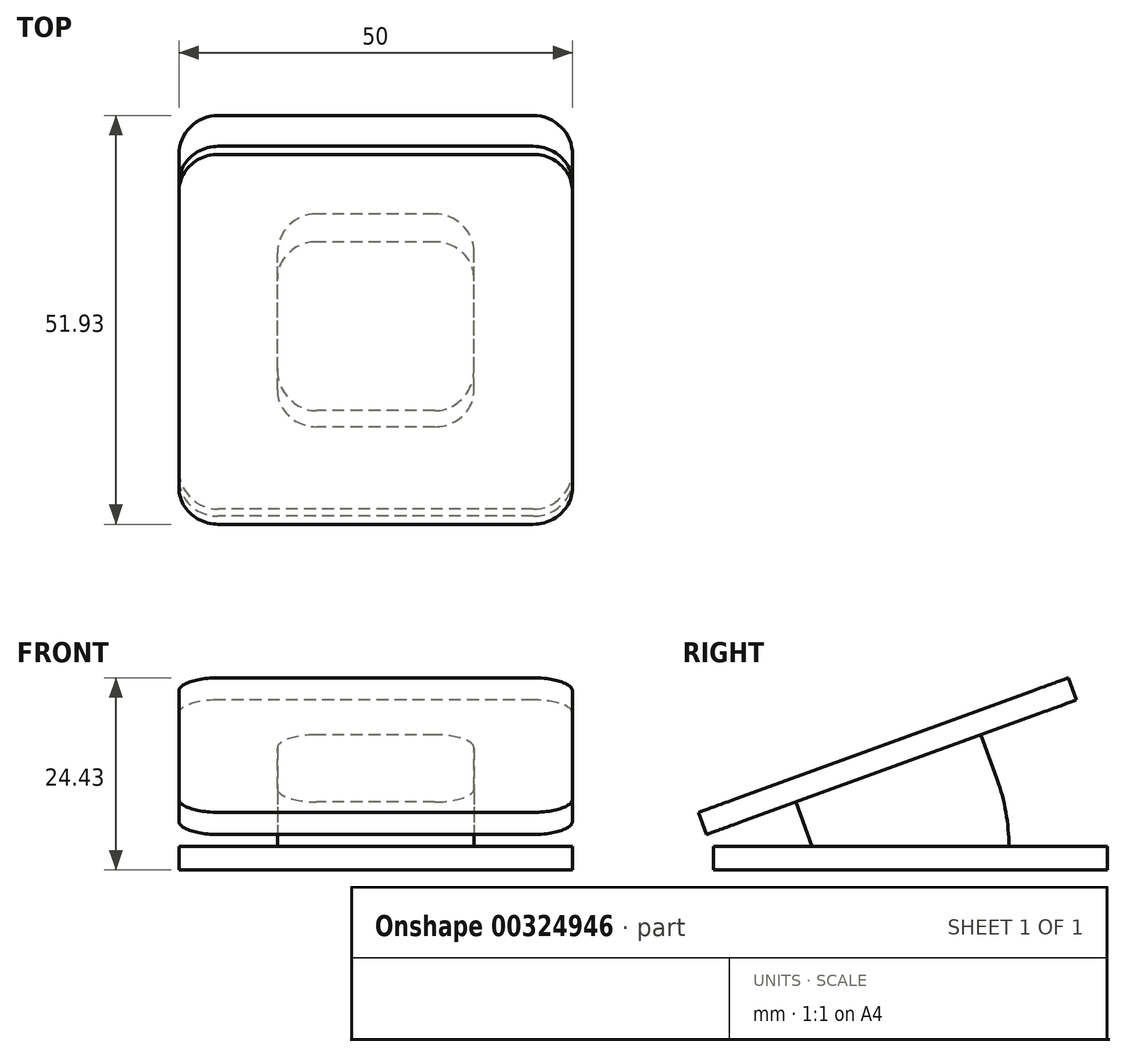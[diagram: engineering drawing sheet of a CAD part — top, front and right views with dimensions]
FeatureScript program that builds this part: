
annotation { "Feature Type Name" : "Feature", "Feature Type Description" : "" }
export const myFeature = defineFeature(function(context is Context, id is Id, definition is map)
    precondition{}
    {
        {
            var Q0;
            Q0=qCreatedBy(makeId("Top.planeOp"),FACE);
            var sketch = newSketch(context, id + "F0", { "sketchPlane" : qUnion([Q0])});
            skLineSegment(sketch, "E0.bottom", {"start": v(25, -25) * mm, "end": v(-25, -25) * mm});
            skLineSegment(sketch, "E0.top", {"start": v(25, 25) * mm, "end": v(-25, 25) * mm});
            skLineSegment(sketch, "E0.left", {"start": v(25, -25) * mm, "end": v(25, 25) * mm});
            skLineSegment(sketch, "E0.right", {"start": v(-25, -25) * mm, "end": v(-25, 25) * mm});
            skPoint(sketch, "E0.middle", {"position": v(0, 0) * mm});
            skSolve(sketch);
        }
        {
            var Q0;
            Q0=makeQuery(id+"F0.imprint","IMPRINT",FACE,{"disambiguationData":[TD([[makeQuery(id+"F0.imprint","IMPRINT",EDGE,{"derivedFrom":sQuery(id+"F0.wireOp",EDGE,"E0.bottom")}),-1.0]])]});
            extrude(context, id + "F1", {"entities" : qUnion([Q0]), "depth" : 3 * mm});
        }
        {
            var Q0;
            Q0=makeQuery(id+"F1.opExtrude","CAP_FACE",FACE,{"disambiguationData":[OSD([sQuery(id+"F0.wireOp",EDGE,"E0.bottom"),sQuery(id+"F0.wireOp",EDGE,"E0.top"),sQuery(id+"F0.wireOp",EDGE,"E0.left"),sQuery(id+"F0.wireOp",EDGE,"E0.right")])],"isStart":false});
            var sketch = newSketch(context, id + "F2", { "sketchPlane" : qUnion([Q0])});
            skLineSegment(sketch, "E1.bottom", {"start": v(12.5, -12.5) * mm, "end": v(-12.5, -12.5) * mm});
            skLineSegment(sketch, "E1.top", {"start": v(12.5, 12.5) * mm, "end": v(-12.5, 12.5) * mm});
            skLineSegment(sketch, "E1.left", {"start": v(12.5, -12.5) * mm, "end": v(12.5, 12.5) * mm});
            skLineSegment(sketch, "E1.right", {"start": v(-12.5, -12.5) * mm, "end": v(-12.5, 12.5) * mm});
            skPoint(sketch, "E1.middle", {"position": v(0, 0) * mm});
            skSolve(sketch);
        }
        {
            var Q0;
            Q0=makeQuery(id+"F2.imprint","IMPRINT",FACE,{"disambiguationData":[TD([[makeQuery(id+"F2.imprint","IMPRINT",EDGE,{"derivedFrom":sQuery(id+"F2.wireOp",EDGE,"E1.bottom")}),-1.0]])]});
            var Q1;
            Q1=sQuery(id+"F2.wireOp",EDGE,"E1.bottom");
            revolve(context, id + "F3", {"operationType" : NewBodyOperationType.ADD, "entities" : qUnion([Q0]), "axis" : qUnion([Q1]), "revolveType" : RevolveType.ONE_DIRECTION, "oppositeDirection" : true, "angle" : 20 * degree});
        }
        {
            var Q0;
            Q0=makeQuery(id+"F3.opRevolve","CAP_FACE",FACE,{"disambiguationData":[OSD([sQuery(id+"F2.wireOp",EDGE,"E1.bottom"),sQuery(id+"F2.wireOp",EDGE,"E1.top"),sQuery(id+"F2.wireOp",EDGE,"E1.left"),sQuery(id+"F2.wireOp",EDGE,"E1.right")])],"isStart":false});
            extrude(context, id + "F4", {"entities" : qUnion([Q0]), "operationType" : NewBodyOperationType.ADD, "depth" : 6 * mm});
        }
        {
            var Q0;
            Q0=makeQuery(id+"F4.opExtrude","CAP_FACE",FACE,{"disambiguationData":[OSD([sQuery(id+"F2.wireOp",EDGE,"E1.bottom"),sQuery(id+"F2.wireOp",EDGE,"E1.top"),sQuery(id+"F2.wireOp",EDGE,"E1.left"),sQuery(id+"F2.wireOp",EDGE,"E1.right")])],"isStart":false});
            var sketch = newSketch(context, id + "F5", { "sketchPlane" : qUnion([Q0])});
            skLineSegment(sketch, "E2.bottom", {"start": v(25, -22.8) * mm, "end": v(-25, -22.8) * mm});
            skLineSegment(sketch, "E2.top", {"start": v(25, 27.2) * mm, "end": v(-25, 27.2) * mm});
            skLineSegment(sketch, "E2.left", {"start": v(25, -22.8) * mm, "end": v(25, 27.2) * mm});
            skLineSegment(sketch, "E2.right", {"start": v(-25, -22.8) * mm, "end": v(-25, 27.2) * mm});
            skPoint(sketch, "E2.middle", {"position": v(0, 2.2) * mm});
            skSolve(sketch);
        }
        {
            var Q0;
            Q0 = qSketchRegion(id + "F5", true);
            extrude(context, id + "F6", {"entities" : qUnion([Q0]), "operationType" : NewBodyOperationType.ADD, "depth" : 3 * mm});
        }
        {
            var Q0;
            Q0=makeQuery(id+"F6.opExtrude","SWEPT_EDGE",EDGE,{"disambiguationData":[OSD([sQuery(id+"F5.wireOp",EDGE,"E2.top"),sQuery(id+"F5.wireOp",EDGE,"E2.left")])]});
            var Q1;
            Q1=makeQuery(id+"F6.opExtrude","SWEPT_EDGE",EDGE,{"disambiguationData":[OSD([sQuery(id+"F5.wireOp",EDGE,"E2.top"),sQuery(id+"F5.wireOp",EDGE,"E2.right")])]});
            var Q2;
            Q2=makeQuery(id+"F6.opExtrude","SWEPT_EDGE",EDGE,{"disambiguationData":[OSD([sQuery(id+"F5.wireOp",EDGE,"E2.bottom"),sQuery(id+"F5.wireOp",EDGE,"E2.right")])]});
            var Q3;
            Q3=makeQuery(id+"F6.opExtrude","SWEPT_EDGE",EDGE,{"disambiguationData":[OSD([sQuery(id+"F5.wireOp",EDGE,"E2.bottom"),sQuery(id+"F5.wireOp",EDGE,"E2.left")])]});
            var Q4;
            Q4=makeQuery(id+"F1.opExtrude","SWEPT_EDGE",EDGE,{"disambiguationData":[OSD([sQuery(id+"F0.wireOp",EDGE,"E0.bottom"),sQuery(id+"F0.wireOp",EDGE,"E0.left")])]});
            var Q5;
            Q5=makeQuery(id+"F1.opExtrude","SWEPT_EDGE",EDGE,{"disambiguationData":[OSD([sQuery(id+"F0.wireOp",EDGE,"E0.bottom"),sQuery(id+"F0.wireOp",EDGE,"E0.right")])]});
            var Q6;
            Q6=makeQuery(id+"F1.opExtrude","SWEPT_EDGE",EDGE,{"disambiguationData":[OSD([sQuery(id+"F0.wireOp",EDGE,"E0.top"),sQuery(id+"F0.wireOp",EDGE,"E0.right")])]});
            var Q7;
            Q7=makeQuery(id+"F1.opExtrude","SWEPT_EDGE",EDGE,{"disambiguationData":[OSD([sQuery(id+"F0.wireOp",EDGE,"E0.top"),sQuery(id+"F0.wireOp",EDGE,"E0.left")])]});
            fillet(context, id + "F7", {"entities" : qUnion([Q0, Q1, Q2, Q3, Q4, Q5, Q6, Q7]), "radius" : 5 * mm, "tangentPropagation" : true, "allowEdgeOverflow" : false});
        }
        {
            var Q0;
            Q0=makeQuery(id+"F4.opExtrude","SWEPT_EDGE",EDGE,{"disambiguationData":[OSD([sQuery(id+"F2.wireOp",EDGE,"E1.top"),sQuery(id+"F2.wireOp",EDGE,"E1.left")])]});
            var Q1;
            Q1=makeQuery(id+"F4.opExtrude","SWEPT_EDGE",EDGE,{"disambiguationData":[OSD([sQuery(id+"F2.wireOp",EDGE,"E1.top"),sQuery(id+"F2.wireOp",EDGE,"E1.right")])]});
            var Q2;
            Q2=makeQuery(id+"F4.opExtrude","SWEPT_EDGE",EDGE,{"disambiguationData":[OSD([sQuery(id+"F2.wireOp",EDGE,"E1.bottom"),sQuery(id+"F2.wireOp",EDGE,"E1.right")])]});
            var Q3;
            Q3=makeQuery(id+"F4.opExtrude","SWEPT_EDGE",EDGE,{"disambiguationData":[OSD([sQuery(id+"F2.wireOp",EDGE,"E1.bottom"),sQuery(id+"F2.wireOp",EDGE,"E1.left")])]});
            fillet(context, id + "F8", {"entities" : qUnion([Q0, Q1, Q2, Q3]), "radius" : 5 * mm, "tangentPropagation" : true, "allowEdgeOverflow" : false});
        }
    });
